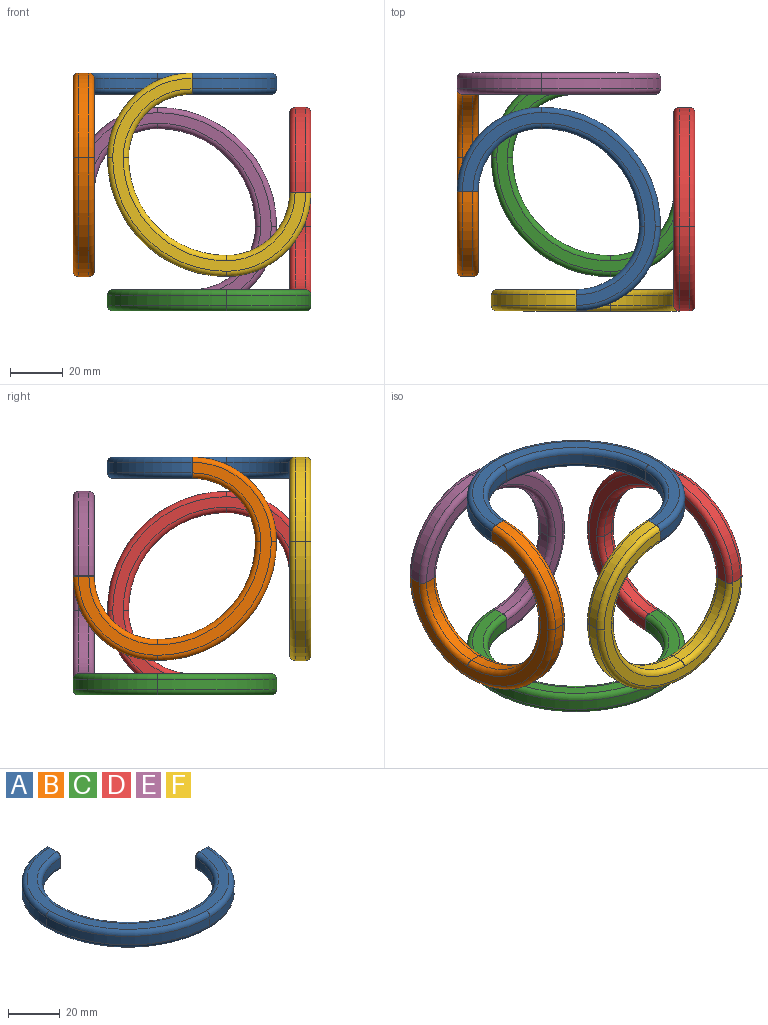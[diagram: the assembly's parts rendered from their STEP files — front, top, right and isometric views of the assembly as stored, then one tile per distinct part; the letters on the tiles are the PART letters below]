
ASSEMBLY  parts=6 mates=5
PART A: 32 faces, bbox 83.3x83.3x8 mm
  f0: plane 8x8mm, normal (1,0,0), area 42.9mm2, adj f4,f5,f8,f9,f15,f16,f17,f18
  f1: plane 8x8mm, normal (0,1,0), area 42.9mm2, adj f2,f3,f4,f5,f10,f11,f12,f13
  f2: cylinder r=32mm len=32mm, axis (0,0,-1), area 201.1mm2, adj f1,f6,f23,f28
  f3: cylinder r=24mm len=24mm, axis (0,0,-1), area 150.8mm2, adj f1,f7,f20,f31
  f4: plane 73x73mm, normal (0,0,1), area 609.5mm2, adj f0,f1,f26,f27,f28,f29,f30,f31
  f5: plane 73x73mm, normal (0,0,-1), area 609.5mm2, adj f0,f1,f20,f21,f22,f23,f24,f25
  f6: cylinder r=45mm len=45mm, axis (0,0,-1), area 282.7mm2, adj f2,f8,f24,f27
  f7: cylinder r=37mm len=37mm, axis (0,0,-1), area 232.5mm2, adj f3,f9,f21,f30
  f8: cylinder r=32mm len=32mm, axis (0,0,-1), area 201.1mm2, adj f0,f6,f25,f26
  f9: cylinder r=24mm len=24mm, axis (0,0,-1), area 150.8mm2, adj f0,f7,f22,f29
  f10: plane 5.5x4.2mm, normal (-1,0,0), area 23.1mm2, adj f1,f11,f13,f14
  f11: plane 5.5x4.2mm, normal (0,0,1), area 23.1mm2, adj f1,f10,f12,f14
  f12: plane 5.5x4.2mm, normal (1,0,0), area 23.1mm2, adj f1,f11,f13,f14
  f13: plane 5.5x4.2mm, normal (0,0,-1), area 23.1mm2, adj f1,f10,f12,f14
  f14: plane 4.2x4.2mm, normal (0,1,0), area 17.6mm2, adj f10,f11,f12,f13
  f15: plane 5.5x4.2mm, normal (0,1,0), area 23.1mm2, adj f0,f16,f18,f19
  f16: plane 5.5x4.2mm, normal (0,0,1), area 23.1mm2, adj f0,f15,f17,f19
  f17: plane 5.5x4.2mm, normal (0,-1,0), area 23.1mm2, adj f0,f16,f18,f19
  f18: plane 5.5x4.2mm, normal (0,0,-1), area 23.1mm2, adj f0,f15,f17,f19
  f19: plane 4.2x4.2mm, normal (1,0,0), area 17.6mm2, adj f15,f16,f17,f18
  f20: torus R=26mm, axis (0,0,1), area 122mm2, adj f1,f3,f5,f21
  f21: torus R=39mm, axis (0,0,1), area 186.2mm2, adj f5,f7,f20,f22
  f22: torus R=26mm, axis (0,0,1), area 122mm2, adj f0,f5,f9,f21
  f23: torus R=30mm, axis (0,0,1), area 154.3mm2, adj f1,f2,f5,f24
  f24: torus R=43mm, axis (0,0,1), area 218.5mm2, adj f5,f6,f23,f25
  f25: torus R=30mm, axis (0,0,1), area 154.3mm2, adj f0,f5,f8,f24
  f26: torus R=30mm, axis (0,0,1), area 154.3mm2, adj f0,f4,f8,f27
  f27: torus R=43mm, axis (0,0,1), area 218.5mm2, adj f4,f6,f26,f28
  f28: torus R=30mm, axis (0,0,1), area 154.3mm2, adj f1,f2,f4,f27
  f29: torus R=26mm, axis (0,0,1), area 122mm2, adj f0,f4,f9,f30
  f30: torus R=39mm, axis (0,0,1), area 186.2mm2, adj f4,f7,f29,f31
  f31: torus R=26mm, axis (0,0,1), area 122mm2, adj f1,f3,f4,f30
PART B: same geometry as A
PART C: same geometry as A
PART D: same geometry as A
PART E: same geometry as A
PART F: same geometry as A
PLACE A rot(axis=(0.71,-0.71,0),180deg) t=(-8,-20,108)mm
PLACE B rot(axis=(0.58,0.58,0.58),120deg) t=(-40,6,76)mm
PLACE C t=(18,6,18)mm
PLACE D rot(axis=(0.71,0,-0.71),180deg) t=(50,-20,50)mm
PLACE E rot(axis=(-0.58,0.58,0.58),120deg) t=(-8,30,50)mm
PLACE F rot(axis=(1,0,0),90deg) t=(18,-44,76)mm
MATE fastened E.f1 <-> C.f0  axis (-1,0,0) through (5,34,22)mm
MATE fastened B.f0 <-> A.f0  axis (0,1,0) through (-36,-7,104)mm
MATE fastened A.f1 <-> F.f0  axis (-1,0,0) through (5,-48,104)mm
MATE fastened F.f1 <-> D.f0  axis (0,0,1) through (46,-48,63)mm
MATE fastened D.f1 <-> C.f1  axis (0,-1,0) through (46,-7,22)mm
